# Revit family: AFX-Tad-LED_Sconce-1
name_source: partatom
category: Lighting Fixtures
units: mm (PartAtom-declared; Revit-internal decimal feet)

## family parameters
Cut with Voids When Loaded = No
Host = Face
Light Source = Yes
Part Type = Normal
Room Calculation Point = No
Round Connector Dimension = Use Diameter
Shared = No

## types (1)
- TADS0514LAJMVBK
    Apparent Load = 0 VA
    Assembly Code = D5020200
    Body Finish = AFX - Paint Finish Black
    Color Filter = 16777215
    Colour Rendering Index = 90
    Default Elevation = 48"
    Depth = 4"
    Description = LED Sconce  - 14"H x 4 1/2"W x 4"D
    Diffuser Finish = AFX - Acrylic
    Dimming Lamp Color Temperature Shift = <None>
    Emit Shape Visible in Rendering = No
    Emit from Rectangle Length = 1 3/4"
    Emit from Rectangle Width = 12"
    Height = 14"
    Housing Finish = AFX - Paint Finish Black
    Keynote = 12500
    Manufacturer = AFX Inc
    Model = TADS0514LAJMVBK
    Photometric Web File = TADS0514LAJUDSN_3000K_IES.IES
    Power Factor = 1
    Product Documentation Link = https://www.afxinc.com
    Revit Model Built By = https://www.servex-us.com
    Sustainability = https://lamprecycle.org
    Tilt Angle = 90.00°
    Type Comments = Tad
    URL = https://www.afxinc.com
    Voltage = 120 V
    Wattage Comments = 12w
    Width = 4 1/2"

## geometry (parser evidence)
native form markers: Sweep x1
no freeform markers — native parametric forms only
